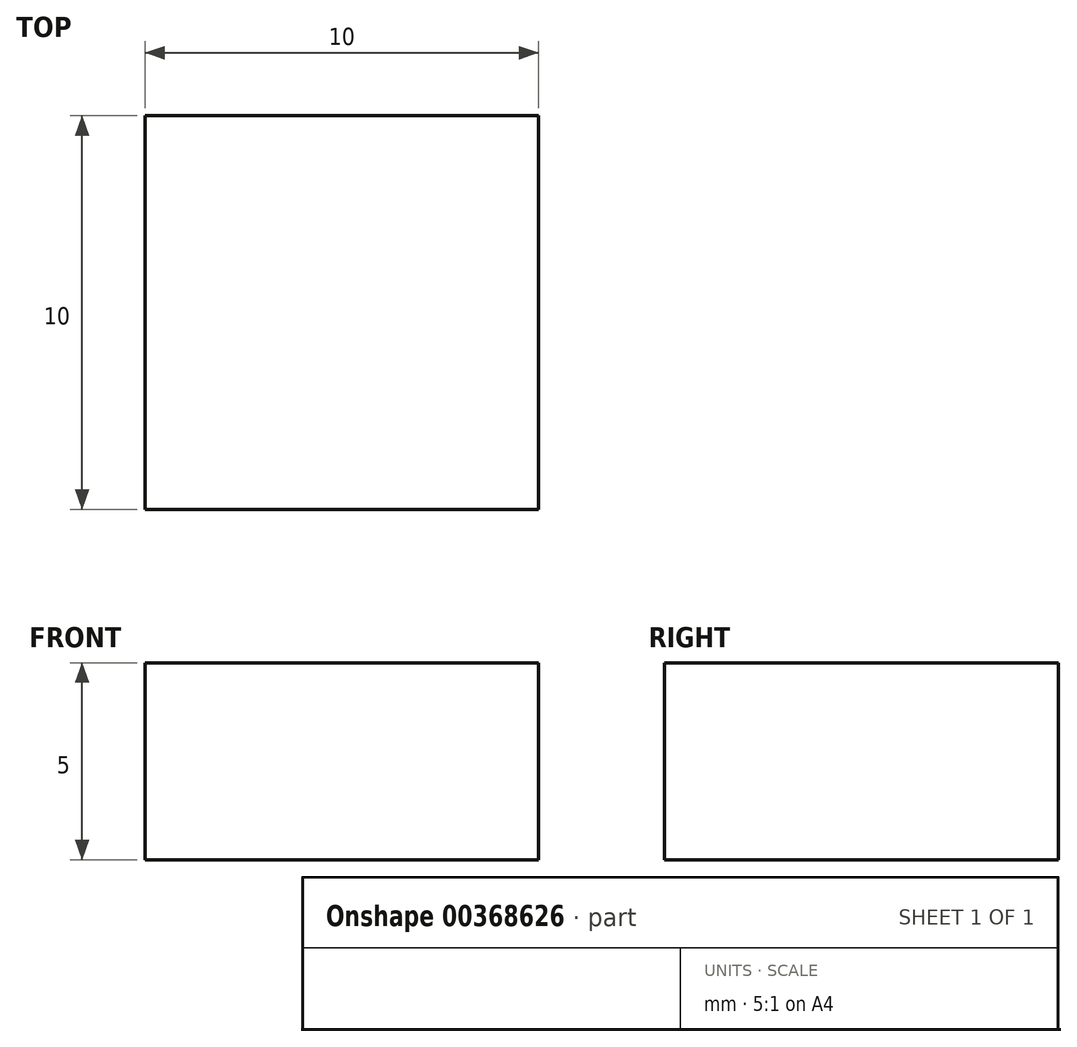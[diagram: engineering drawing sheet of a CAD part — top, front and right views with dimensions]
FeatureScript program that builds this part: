
annotation { "Feature Type Name" : "Feature", "Feature Type Description" : "" }
export const myFeature = defineFeature(function(context is Context, id is Id, definition is map)
    precondition{}
    {
        {
            var Q0;
            Q0=qCreatedBy(makeId("Front.planeOp"),FACE);
            var sketch = newSketch(context, id + "F0", { "sketchPlane" : qUnion([Q0])});
            skLineSegment(sketch, "E0.bottom", {"start": v(0, 0) * mm, "end": v(10, 0) * mm});
            skLineSegment(sketch, "E0.top", {"start": v(0, 5) * mm, "end": v(10, 5) * mm});
            skLineSegment(sketch, "E0.left", {"start": v(0, 0) * mm, "end": v(0, 5) * mm});
            skLineSegment(sketch, "E0.right", {"start": v(10, 0) * mm, "end": v(10, 5) * mm});
            skSolve(sketch);
        }
        {
            var Q0;
            Q0 = qSketchRegion(id + "F0", true);
            extrude(context, id + "F1", {"entities" : qUnion([Q0]), "depth" : 10 * mm});
        }
    });
